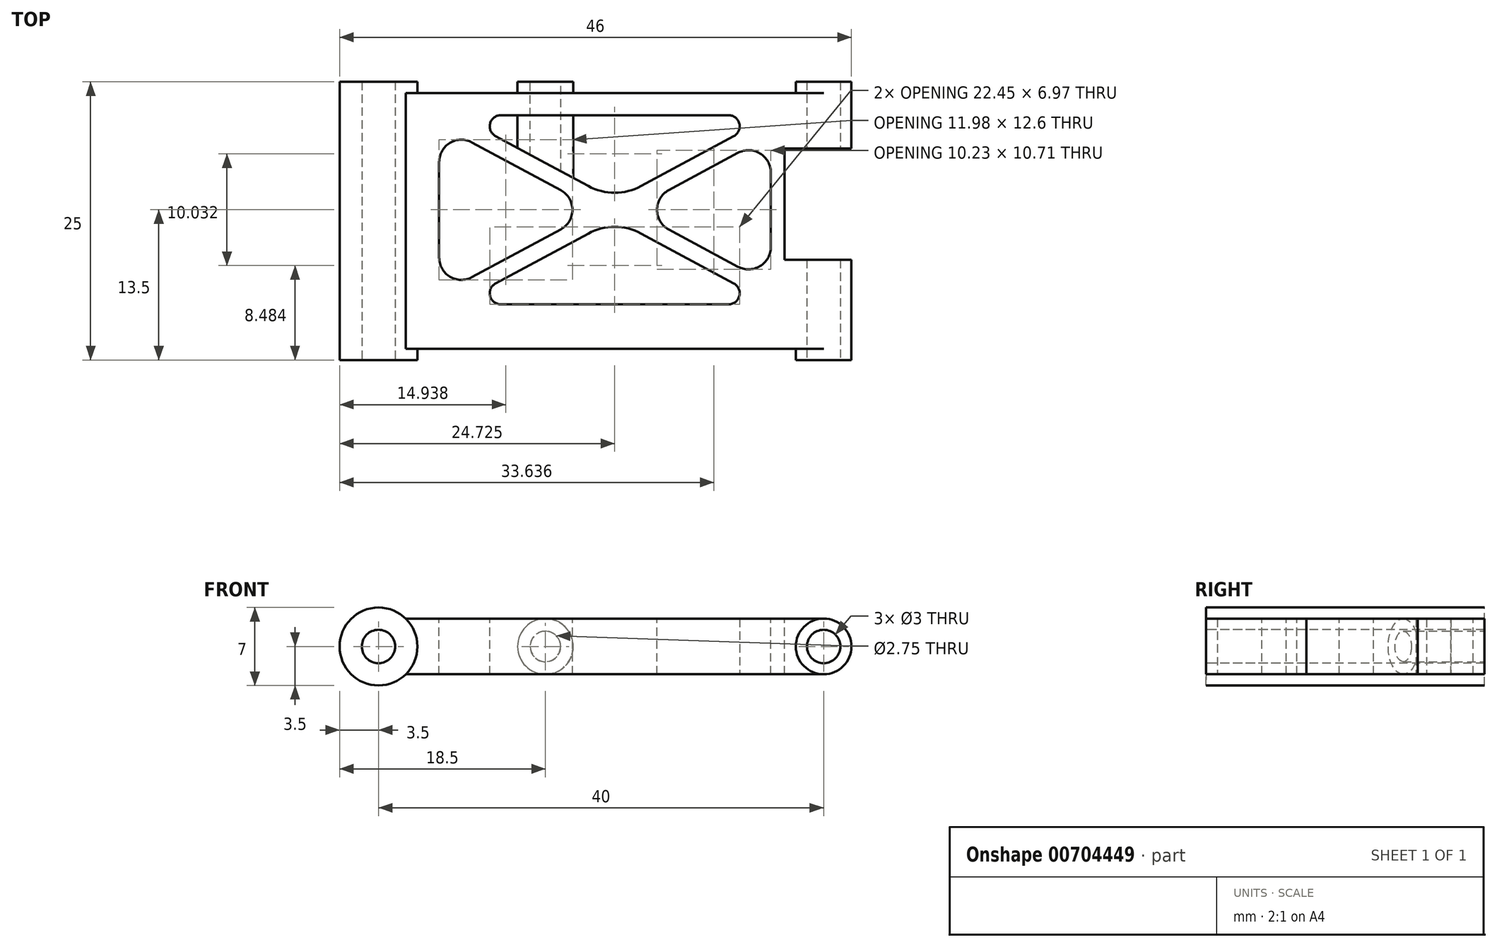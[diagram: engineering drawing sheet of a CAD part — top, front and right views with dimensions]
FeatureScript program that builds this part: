
annotation { "Feature Type Name" : "Feature", "Feature Type Description" : "" }
export const myFeature = defineFeature(function(context is Context, id is Id, definition is map)
    precondition{}
    {
        {
            var Q0;
            Q0=qCreatedBy(makeId("Front.planeOp"),FACE);
            var sketch = newSketch(context, id + "F0", { "sketchPlane" : qUnion([Q0])});
            skCircle(sketch, "E0", {"center": v(0, 0) * mm, "radius": 1.5 * mm});
            skCircle(sketch, "E1", {"center": v(0, 0) * mm, "radius": 3.5 * mm});
            skLineSegment(sketch, "E2", {"start": v(2.45, 2.5) * mm, "end": v(40, 2.5) * mm});
            skLineSegment(sketch, "E3.MirrorCS", {"start": v(2.45, -2.5) * mm, "end": v(40, -2.5) * mm});
            skCircle(sketch, "E4", {"center": v(40, 0) * mm, "radius": 1.5 * mm});
            skCircle(sketch, "E5", {"center": v(40, 0) * mm, "radius": 2.5 * mm});
            skSolve(sketch);
        }
        {
            var Q0;
            Q0=makeQuery(id+"F0.imprint","IMPRINT",FACE,{"disambiguationData":[TD([[makeQuery(id+"F0.imprint","IMPRINT",EDGE,{"derivedFrom":sQuery(id+"F0.wireOp",EDGE,"E0")}),-1.0]])]});
            var Q1;
            {var subQ1=sQuery(id+"F0.wireOp",EDGE,"E2");Q1=makeQuery(id+"F0.imprint","IMPRINT",FACE,{"disambiguationData":[TD([[makeQuery(id+"F0.imprint","IMPRINT",EDGE,{"derivedFrom":subQ1}),-1.0]])]});}
            var Q2;
            Q2=makeQuery(id+"F0.imprint","IMPRINT",FACE,{"disambiguationData":[TD([[makeQuery(id+"F0.imprint","IMPRINT",EDGE,{"derivedFrom":sQuery(id+"F0.wireOp",EDGE,"E4")}),-1.0]])]});
            extrude(context, id + "F1", {"entities" : qUnion([Q0, Q1, Q2]), "oppositeDirection" : true, "depth" : 25 * mm, "offsetDistance" : 25 * mm});
        }
        {
            var Q0;
            {var subQ1=sQuery(id+"F0.wireOp",EDGE,"E2");Q0=makeQuery(id+"F0.imprint","IMPRINT",FACE,{"disambiguationData":[TD([[makeQuery(id+"F0.imprint","IMPRINT",EDGE,{"derivedFrom":subQ1}),-1.0]])]});}
            extrude(context, id + "F2", {"entities" : qUnion([Q0]), "operationType" : NewBodyOperationType.REMOVE, "oppositeDirection" : true, "depth" : 1 * mm, "offsetDistance" : 25 * mm});
        }
        {
            var Q0;
            Q0=makeQuery(id+"F1.opExtrude","SWEPT_FACE",FACE,{"disambiguationData":[OSD([sQuery(id+"F0.wireOp",EDGE,"E2")])]});
            var sketch = newSketch(context, id + "F3", { "sketchPlane" : qUnion([Q0])});
            skLineSegment(sketch, "E6", {"start": v(5.45, 5) * mm, "end": v(37, 5) * mm});
            skLineSegment(sketch, "E7", {"start": v(37, 5) * mm, "end": v(37, 9) * mm});
            skLineSegment(sketch, "E8", {"start": v(37, 22) * mm, "end": v(5.45, 22) * mm});
            skLineSegment(sketch, "E9", {"start": v(5.45, 22) * mm, "end": v(5.45, 5) * mm});
            skLineSegment(sketch, "E10", {"start": v(42.5, 19) * mm, "end": v(42.5, 9) * mm});
            skLineSegment(sketch, "E11", {"start": v(36.5, 19) * mm, "end": v(42.5, 19) * mm});
            skLineSegment(sketch, "E12", {"start": v(36.5, 9) * mm, "end": v(42.5, 9) * mm});
            skLineSegment(sketch, "E13.trimOffspring", {"start": v(37, 19) * mm, "end": v(37, 22) * mm});
            skLineSegment(sketch, "E14", {"start": v(35.42, 22) * mm, "end": v(5.45, 5.85) * mm});
            skLineSegment(sketch, "E15", {"start": v(7.03, 5) * mm, "end": v(37, 21.15) * mm});
            skLineSegment(sketch, "E16", {"start": v(21.22, 22) * mm, "end": v(21.22, 5) * mm, "construction": true});
            skLineSegment(sketch, "E17", {"start": v(5.45, 5) * mm, "end": v(37, 22) * mm, "construction": true});
            skLineSegment(sketch, "E18.MirrorCS", {"start": v(7.03, 22) * mm, "end": v(37, 5.85) * mm});
            skLineSegment(sketch, "E19.MirrorCS", {"start": v(35.42, 5) * mm, "end": v(5.45, 21.15) * mm});
            skLineSegment(sketch, "E20", {"start": v(36.5, 20.88) * mm, "end": v(36.5, 6.12) * mm});
            skLineSegment(sketch, "E21", {"start": v(35.25, 20.2) * mm, "end": v(35.25, 6.8) * mm});
            skSolve(sketch);
        }
        {
            var Q0;
            {var subQ0=sQuery(id+"F3.wireOp",EDGE,"E14");var subQ1=sQuery(id+"F3.wireOp",EDGE,"E9");var subQ2=makeQuery(id+"F3.imprint","INTERSECT",VERTEX,{"derivedFrom":[subQ1,subQ0]});Q0=makeQuery(id+"F3.imprint","IMPRINT",FACE,{"disambiguationData":[TD([[makeQuery(id+"F3.imprint","IMPRINT",EDGE,{"disambiguationData":[TD([[subQ2,1.0]])],"derivedFrom":subQ1}),1.0]])]});}
            var Q1;
            {var subQ0=sQuery(id+"F3.wireOp",EDGE,"E14");var subQ1=sQuery(id+"F3.wireOp",EDGE,"E8");var subQ2=makeQuery(id+"F3.imprint","INTERSECT",VERTEX,{"derivedFrom":[subQ1,subQ0]});Q1=makeQuery(id+"F3.imprint","IMPRINT",FACE,{"disambiguationData":[TD([[makeQuery(id+"F3.imprint","IMPRINT",EDGE,{"disambiguationData":[TD([[subQ2,-1.0]])],"derivedFrom":subQ1}),1.0]])]});}
            var Q2;
            {var subQ0=sQuery(id+"F3.wireOp",EDGE,"E15");var subQ1=sQuery(id+"F3.wireOp",EDGE,"E6");var subQ2=makeQuery(id+"F3.imprint","INTERSECT",VERTEX,{"derivedFrom":[subQ1,subQ0]});Q2=makeQuery(id+"F3.imprint","IMPRINT",FACE,{"disambiguationData":[TD([[makeQuery(id+"F3.imprint","IMPRINT",EDGE,{"disambiguationData":[TD([[subQ2,-1.0]])],"derivedFrom":subQ1}),1.0]])]});}
            var Q3;
            {var subQ0=sQuery(id+"F3.wireOp",EDGE,"E21");Q3=makeQuery(id+"F3.imprint","IMPRINT",FACE,{"disambiguationData":[TD([[makeQuery(id+"F3.imprint","IMPRINT",EDGE,{"derivedFrom":subQ0}),-1.0]])]});}
            var Q4;
            {var subQ4=sQuery(id+"F3.wireOp",EDGE,"E20");var subQ6=sQuery(id+"F3.wireOp",EDGE,"E11");var subQ7=makeQuery(id+"F3.imprint","INTERSECT",VERTEX,{"derivedFrom":[subQ6,subQ4]});Q4=makeQuery(id+"F3.imprint","IMPRINT",FACE,{"disambiguationData":[TD([[makeQuery(id+"F3.imprint","IMPRINT",EDGE,{"disambiguationData":[TD([[subQ7,-1.0]])],"derivedFrom":subQ6}),-1.0]])]});}
            var Q5;
            {var subQ0=sQuery(id+"F3.wireOp",EDGE,"E10");Q5=makeQuery(id+"F3.imprint","IMPRINT",FACE,{"disambiguationData":[TD([[makeQuery(id+"F3.imprint","IMPRINT",EDGE,{"derivedFrom":subQ0}),-1.0]])]});}
            extrude(context, id + "F4", {"entities" : qUnion([Q0, Q1, Q2, Q3, Q4, Q5]), "operationType" : NewBodyOperationType.REMOVE, "oppositeDirection" : true, "depth" : 25 * mm, "offsetDistance" : 25 * mm});
        }
        {
            var Q0;
            Q0=makeQuery(id+"F4.boolean.opBoolean","COPY",EDGE,{"derivedFrom":makeQuery(id+"F4.opExtrude","SWEPT_EDGE",EDGE,{"disambiguationData":[OSD([sQuery(id+"F3.wireOp",EDGE,"E14"),sQuery(id+"F3.wireOp",EDGE,"E18.MirrorCS")])]})});
            var Q1;
            Q1=makeQuery(id+"F4.boolean.opBoolean","COPY",EDGE,{"derivedFrom":makeQuery(id+"F4.opExtrude","SWEPT_EDGE",EDGE,{"disambiguationData":[OSD([sQuery(id+"F3.wireOp",EDGE,"E15"),sQuery(id+"F3.wireOp",EDGE,"E19.MirrorCS")])]})});
            fillet(context, id + "F5", {"entities" : qUnion([Q0, Q1]), "tangentPropagation" : true, "radius" : 5 * mm, "defaultsChanged" : false, "vertexSettings" : [], "allowEdgeOverflow" : false});
        }
        {
            var Q0;
            Q0=makeQuery(id+"F4.boolean.opBoolean","COPY",EDGE,{"derivedFrom":makeQuery(id+"F4.opExtrude","SWEPT_EDGE",EDGE,{"disambiguationData":[OSD([sQuery(id+"F3.wireOp",EDGE,"E9"),sQuery(id+"F3.wireOp",EDGE,"E19.MirrorCS")])]})});
            var Q1;
            Q1=makeQuery(id+"F4.boolean.opBoolean","COPY",EDGE,{"derivedFrom":makeQuery(id+"F4.opExtrude","SWEPT_EDGE",EDGE,{"disambiguationData":[OSD([sQuery(id+"F3.wireOp",EDGE,"E9"),sQuery(id+"F3.wireOp",EDGE,"E14")])]})});
            var Q2;
            Q2=makeQuery(id+"F4.boolean.opBoolean","COPY",EDGE,{"derivedFrom":makeQuery(id+"F4.opExtrude","SWEPT_EDGE",EDGE,{"disambiguationData":[OSD([sQuery(id+"F3.wireOp",EDGE,"E18.MirrorCS"),sQuery(id+"F3.wireOp",EDGE,"E21")])]})});
            var Q3;
            Q3=makeQuery(id+"F4.boolean.opBoolean","COPY",EDGE,{"derivedFrom":makeQuery(id+"F4.opExtrude","SWEPT_EDGE",EDGE,{"disambiguationData":[OSD([sQuery(id+"F3.wireOp",EDGE,"E15"),sQuery(id+"F3.wireOp",EDGE,"E21")])]})});
            var Q4;
            Q4=makeQuery(id+"F4.boolean.opBoolean","COPY",EDGE,{"derivedFrom":makeQuery(id+"F4.opExtrude","SWEPT_EDGE",EDGE,{"disambiguationData":[OSD([sQuery(id+"F3.wireOp",EDGE,"E15"),sQuery(id+"F3.wireOp",EDGE,"E18.MirrorCS")])]})});
            var Q5;
            Q5=makeQuery(id+"F4.boolean.opBoolean","COPY",EDGE,{"derivedFrom":makeQuery(id+"F4.opExtrude","SWEPT_EDGE",EDGE,{"disambiguationData":[OSD([sQuery(id+"F3.wireOp",EDGE,"E14"),sQuery(id+"F3.wireOp",EDGE,"E19.MirrorCS")])]})});
            fillet(context, id + "F6", {"entities" : qUnion([Q0, Q1, Q2, Q3, Q4, Q5]), "tangentPropagation" : true, "radius" : 2 * mm, "defaultsChanged" : false, "vertexSettings" : [], "allowEdgeOverflow" : false});
        }
        {
            var Q0;
            Q0=makeQuery(id+"F4.boolean.opBoolean","COPY",EDGE,{"derivedFrom":makeQuery(id+"F4.opExtrude","SWEPT_EDGE",EDGE,{"disambiguationData":[OSD([sQuery(id+"F3.wireOp",EDGE,"E8"),sQuery(id+"F3.wireOp",EDGE,"E18.MirrorCS")])]})});
            var Q1;
            Q1=makeQuery(id+"F4.boolean.opBoolean","COPY",EDGE,{"derivedFrom":makeQuery(id+"F4.opExtrude","SWEPT_EDGE",EDGE,{"disambiguationData":[OSD([sQuery(id+"F3.wireOp",EDGE,"E8"),sQuery(id+"F3.wireOp",EDGE,"E14")])]})});
            var Q2;
            Q2=makeQuery(id+"F4.boolean.opBoolean","COPY",EDGE,{"derivedFrom":makeQuery(id+"F4.opExtrude","SWEPT_EDGE",EDGE,{"disambiguationData":[OSD([sQuery(id+"F3.wireOp",EDGE,"E6"),sQuery(id+"F3.wireOp",EDGE,"E15")])]})});
            var Q3;
            Q3=makeQuery(id+"F4.boolean.opBoolean","COPY",EDGE,{"derivedFrom":makeQuery(id+"F4.opExtrude","SWEPT_EDGE",EDGE,{"disambiguationData":[OSD([sQuery(id+"F3.wireOp",EDGE,"E6"),sQuery(id+"F3.wireOp",EDGE,"E19.MirrorCS")])]})});
            fillet(context, id + "F7", {"entities" : qUnion([Q0, Q1, Q2, Q3]), "tangentPropagation" : true, "radius" : 1 * mm, "defaultsChanged" : false, "vertexSettings" : [], "allowEdgeOverflow" : false});
        }
        {
            var Q0;
            Q0=makeQuery(id+"F1.opExtrude","CAP_FACE",FACE,{"disambiguationData":[OSD([sQuery(id+"F0.wireOp",EDGE,"E0"),sQuery(id+"F0.wireOp",EDGE,"E1"),sQuery(id+"F0.wireOp",EDGE,"E2"),sQuery(id+"F0.wireOp",EDGE,"E3.MirrorCS"),sQuery(id+"F0.wireOp",EDGE,"E4"),sQuery(id+"F0.wireOp",EDGE,"E5")])],"isStart":false});
            var sketch = newSketch(context, id + "F8", { "sketchPlane" : qUnion([Q0])});
            skCircle(sketch, "E22", {"center": v(-15, 0) * mm, "radius": 1.38 * mm});
            skCircle(sketch, "E23", {"center": v(-15, 0) * mm, "radius": 2.5 * mm});
            skLineSegment(sketch, "E24.0", {"start": v(-2.45, 2.5) * mm, "end": v(-40, 2.5) * mm});
            skCircle(sketch, "E25.0", {"center": v(0, 0) * mm, "radius": 3.5 * mm});
            skLineSegment(sketch, "E26.0", {"start": v(-2.45, -2.5) * mm, "end": v(-40, -2.5) * mm});
            skCircle(sketch, "E27.0", {"center": v(-40, 0) * mm, "radius": 2.5 * mm});
            skSolve(sketch);
        }
        {
            var Q0;
            {var subQ0=sQuery(id+"F8.wireOp",EDGE,"E24.0");var subQ1=sQuery(id+"F8.wireOp",EDGE,"E23");var subQ2=makeQuery(id+"F8.imprint","INTERSECT",VERTEX,{"derivedFrom":[subQ1,subQ0]});Q0=makeQuery(id+"F8.imprint","IMPRINT",FACE,{"disambiguationData":[TD([[makeQuery(id+"F8.imprint","IMPRINT",EDGE,{"disambiguationData":[TD([[subQ2,-1.0]])],"derivedFrom":subQ1}),-1.0]])]});}
            var Q1;
            {var subQ0=sQuery(id+"F8.wireOp",EDGE,"E24.0");var subQ1=sQuery(id+"F8.wireOp",EDGE,"E23");var subQ2=makeQuery(id+"F8.imprint","INTERSECT",VERTEX,{"derivedFrom":[subQ1,subQ0]});Q1=makeQuery(id+"F8.imprint","IMPRINT",FACE,{"disambiguationData":[TD([[makeQuery(id+"F8.imprint","IMPRINT",EDGE,{"disambiguationData":[TD([[subQ2,1.0]])],"derivedFrom":subQ1}),-1.0]])]});}
            extrude(context, id + "F9", {"entities" : qUnion([Q0, Q1]), "operationType" : NewBodyOperationType.REMOVE, "oppositeDirection" : true, "depth" : 1 * mm, "offsetDistance" : 25 * mm});
        }
        {
            var Q0;
            Q0=makeQuery(id+"F8.imprint","IMPRINT",FACE,{"disambiguationData":[TD([[makeQuery(id+"F8.imprint","IMPRINT",EDGE,{"derivedFrom":sQuery(id+"F8.wireOp",EDGE,"E22")}),-1.0]])]});
            var Q1;
            {var subQ0=sQuery(id+"F3.wireOp",EDGE,"E18.MirrorCS");Q1=makeQuery(id+"F4.boolean.opBoolean","COPY",FACE,{"derivedFrom":makeQuery(id+"F4.opExtrude","SWEPT_FACE",FACE,{"disambiguationData":[OSD([subQ0]),TDD([makeQuery(id+"F3.imprint","IMPRINT",EDGE,{"disambiguationData":[TD([[makeQuery(id+"F3.imprint","INTERSECT",VERTEX,{"derivedFrom":[sQuery(id+"F3.wireOp",EDGE,"E8"),subQ0]}),-1.0]])],"derivedFrom":subQ0})])]})});}
            extrude(context, id + "F10", {"entities" : qUnion([Q0]), "operationType" : NewBodyOperationType.ADD, "endBound" : BoundingType.UP_TO_SURFACE, "oppositeDirection" : true, "depth" : 25 * mm, "endBoundEntityFace" : qUnion([Q1]), "offsetDistance" : 25 * mm});
        }
        {
            var Q0;
            Q0=makeQuery(id+"F8.imprint","IMPRINT",FACE,{"disambiguationData":[TD([[makeQuery(id+"F8.imprint","IMPRINT",EDGE,{"derivedFrom":sQuery(id+"F8.wireOp",EDGE,"E22")}),1.0]])]});
            var Q1;
            {var subQ0=sQuery(id+"F3.wireOp",EDGE,"E18.MirrorCS");var subQ1=sQuery(id+"F3.wireOp",EDGE,"E14");var subQ2=makeQuery(id+"F4.boolean.opBoolean","COPY",FACE,{"derivedFrom":makeQuery(id+"F4.opExtrude","SWEPT_FACE",FACE,{"disambiguationData":[OSD([subQ0]),TDD([makeQuery(id+"F3.imprint","IMPRINT",EDGE,{"disambiguationData":[TD([[makeQuery(id+"F3.imprint","INTERSECT",VERTEX,{"derivedFrom":[sQuery(id+"F3.wireOp",EDGE,"E8"),subQ0]}),-1.0]])],"derivedFrom":subQ0})])]})});Q1=makeQuery(id+"F10.boolean.opBoolean","SPLIT",FACE,{"disambiguationData":[TD([makeQuery(id+"F5.opFillet","BLEND_FACE",FACE,{"disambiguationData":[OSD([subQ1,subQ0])]})])],"derivedFrom":subQ2});}
            extrude(context, id + "F11", {"entities" : qUnion([Q0]), "operationType" : NewBodyOperationType.REMOVE, "endBound" : BoundingType.UP_TO_SURFACE, "oppositeDirection" : true, "depth" : 25 * mm, "endBoundEntityFace" : qUnion([Q1]), "offsetDistance" : 25 * mm});
        }
    });
